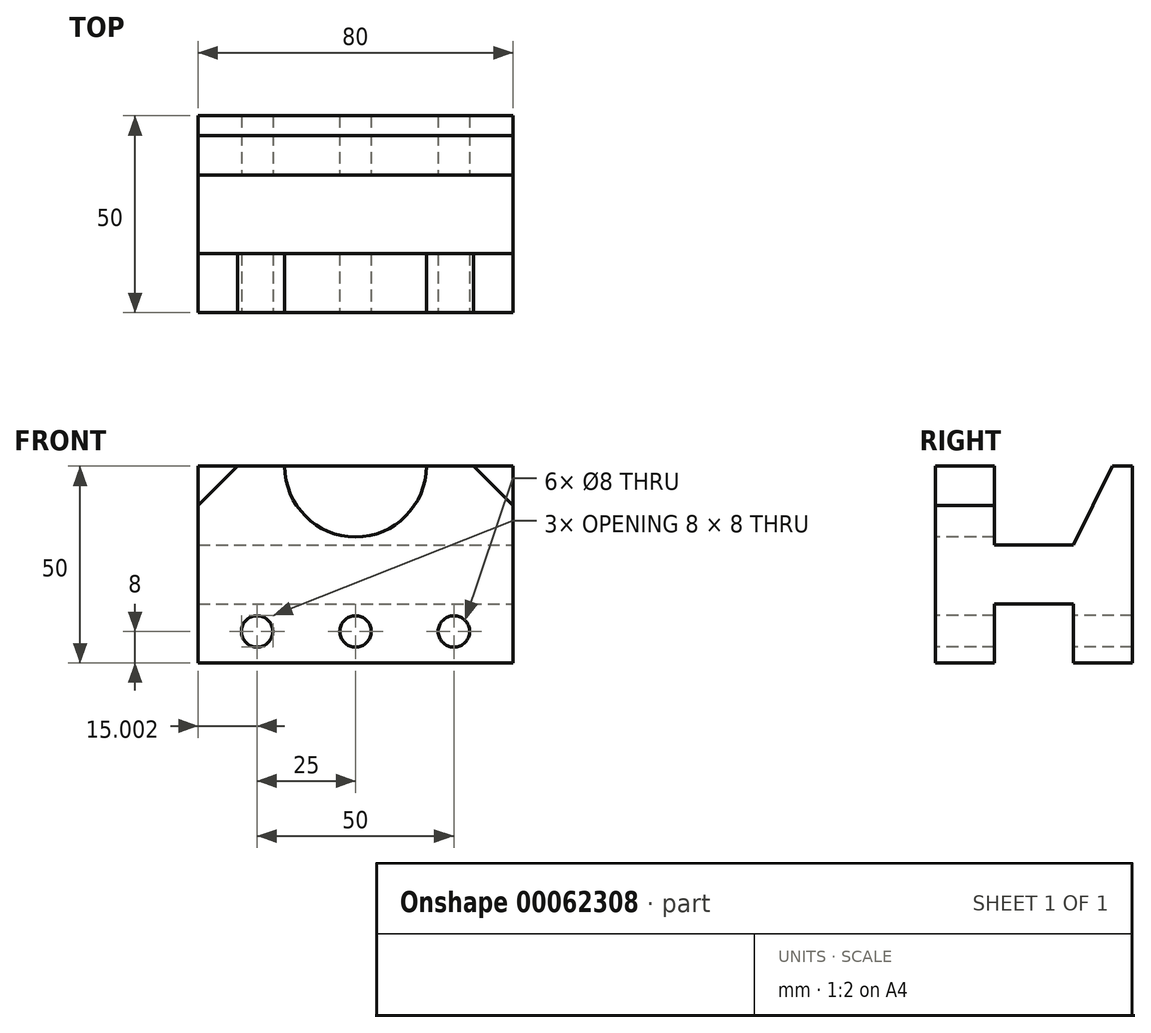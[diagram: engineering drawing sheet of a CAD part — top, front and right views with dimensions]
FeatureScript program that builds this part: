
annotation { "Feature Type Name" : "Feature", "Feature Type Description" : "" }
export const myFeature = defineFeature(function(context is Context, id is Id, definition is map)
    precondition{}
    {
        {
            var Q0;
            Q0=qCreatedBy(makeId("Top.planeOp"),FACE);
            var sketch = newSketch(context, id + "F0", { "sketchPlane" : qUnion([Q0])});
            skLineSegment(sketch, "E0.bottom", {"start": v(3.03, 0) * mm, "end": v(83.03, 0) * mm});
            skLineSegment(sketch, "E0.top", {"start": v(3.03, 50) * mm, "end": v(83.03, 50) * mm});
            skLineSegment(sketch, "E0.left", {"start": v(3.03, 0) * mm, "end": v(3.03, 50) * mm});
            skLineSegment(sketch, "E0.right", {"start": v(83.03, 0) * mm, "end": v(83.03, 50) * mm});
            skSolve(sketch);
        }
        {
            var Q0;
            Q0=makeQuery(id+"F0.imprint","IMPRINT",FACE,{"disambiguationData":[TD([[makeQuery(id+"F0.imprint","IMPRINT",EDGE,{"derivedFrom":sQuery(id+"F0.wireOp",EDGE,"E0.bottom")}),1.0]])]});
            extrude(context, id + "F1", {"entities" : qUnion([Q0]), "depth" : 50 * mm});
        }
        {
            var Q0;
            Q0=makeQuery(id+"F1.opExtrude","SWEPT_FACE",FACE,{"disambiguationData":[OSD([sQuery(id+"F0.wireOp",EDGE,"E0.right")])]});
            var sketch = newSketch(context, id + "F2", { "sketchPlane" : qUnion([Q0])});
            skLineSegment(sketch, "E1.bottom", {"start": v(15, 0) * mm, "end": v(35, 0) * mm});
            skLineSegment(sketch, "E1.top", {"start": v(15, 15) * mm, "end": v(35, 15) * mm});
            skLineSegment(sketch, "E1.left", {"start": v(15, 0) * mm, "end": v(15, 15) * mm});
            skLineSegment(sketch, "E1.right", {"start": v(35, 0) * mm, "end": v(35, 15) * mm});
            skSolve(sketch);
        }
        {
            var Q0;
            Q0=makeQuery(id+"F2.imprint","IMPRINT",FACE,{"disambiguationData":[TD([[makeQuery(id+"F2.imprint","IMPRINT",EDGE,{"derivedFrom":sQuery(id+"F2.wireOp",EDGE,"E1.bottom")}),1.0]])]});
            extrude(context, id + "F3", {"entities" : qUnion([Q0]), "operationType" : NewBodyOperationType.REMOVE, "oppositeDirection" : true, "depth" : 80 * mm});
        }
        {
            var Q0;
            Q0=makeQuery(id+"F1.opExtrude","SWEPT_FACE",FACE,{"disambiguationData":[OSD([sQuery(id+"F0.wireOp",EDGE,"E0.right")])]});
            var sketch = newSketch(context, id + "F4", { "sketchPlane" : qUnion([Q0])});
            skLineSegment(sketch, "E2.bottom", {"start": v(15, 50) * mm, "end": v(45, 50) * mm});
            skLineSegment(sketch, "E2.top", {"start": v(15, 30) * mm, "end": v(35, 30) * mm});
            skLineSegment(sketch, "E2.left", {"start": v(15, 50) * mm, "end": v(15, 30) * mm});
            skLineSegment(sketch, "E3", {"start": v(35, 30) * mm, "end": v(45, 50) * mm});
            skSolve(sketch);
        }
        {
            var Q0;
            Q0=makeQuery(id+"F4.imprint","IMPRINT",FACE,{"disambiguationData":[TD([[makeQuery(id+"F4.imprint","IMPRINT",EDGE,{"derivedFrom":sQuery(id+"F4.wireOp",EDGE,"E2.bottom")}),-1.0]])]});
            extrude(context, id + "F5", {"entities" : qUnion([Q0]), "operationType" : NewBodyOperationType.REMOVE, "oppositeDirection" : true, "depth" : 80 * mm});
        }
        {
            var Q0;
            Q0=makeQuery(id+"F1.opExtrude","SWEPT_FACE",FACE,{"disambiguationData":[OSD([sQuery(id+"F0.wireOp",EDGE,"E0.bottom")])]});
            var sketch = newSketch(context, id + "F6", { "sketchPlane" : qUnion([Q0])});
            skArc(sketch, "E4", {"start": v(25.03, 50) * mm, "mid": v(43.03, 32) * mm, "end": v(61.03, 50) * mm});
            skLineSegment(sketch, "E5", {"start": v(25.03, 50) * mm, "end": v(61.03, 50) * mm});
            skSolve(sketch);
        }
        {
            var Q0;
            Q0 = qSketchRegion(id + "F6", true);
            extrude(context, id + "F7", {"entities" : qUnion([Q0]), "operationType" : NewBodyOperationType.REMOVE, "oppositeDirection" : true, "depth" : 25 * mm});
        }
        {
            var Q0;
            {var subQ0=sQuery(id+"F0.wireOp",EDGE,"E0.bottom");var subQ1=sQuery(id+"F0.wireOp",EDGE,"E0.right");Q0=makeQuery(id+"F5.boolean.opBoolean","SPLIT",EDGE,{"disambiguationData":[TD([makeQuery(id+"F1.opExtrude","SWEPT_FACE",FACE,{"disambiguationData":[OSD([subQ0])]})])],"derivedFrom":makeQuery(id+"F1.opExtrude","CAP_EDGE",EDGE,{"disambiguationData":[OSD([subQ1])],"isStart":false})});}
            chamfer(context, id + "F8", {"entities" : qUnion([Q0]), "width" : 10 * mm, "tangentPropagation" : true});
        }
        {
            var Q0;
            {var subQ0=sQuery(id+"F0.wireOp",EDGE,"E0.bottom");var subQ1=sQuery(id+"F0.wireOp",EDGE,"E0.left");Q0=makeQuery(id+"F5.boolean.opBoolean","SPLIT",EDGE,{"disambiguationData":[TD([makeQuery(id+"F1.opExtrude","SWEPT_FACE",FACE,{"disambiguationData":[OSD([subQ0])]})])],"derivedFrom":makeQuery(id+"F1.opExtrude","CAP_EDGE",EDGE,{"disambiguationData":[OSD([subQ1])],"isStart":false})});}
            chamfer(context, id + "F9", {"entities" : qUnion([Q0]), "width" : 10 * mm, "tangentPropagation" : true});
        }
        {
            var Q0;
            Q0=makeQuery(id+"F1.opExtrude","SWEPT_FACE",FACE,{"disambiguationData":[OSD([sQuery(id+"F0.wireOp",EDGE,"E0.bottom")])]});
            var sketch = newSketch(context, id + "F10", { "sketchPlane" : qUnion([Q0])});
            skCircle(sketch, "E6", {"center": v(18.03, 8) * mm, "radius": 4 * mm});
            skCircle(sketch, "E7", {"center": v(43.03, 8) * mm, "radius": 4 * mm});
            skCircle(sketch, "E8", {"center": v(68.03, 8) * mm, "radius": 4 * mm});
            skSolve(sketch);
        }
        {
            var Q0;
            Q0=makeQuery(id+"F10.imprint","IMPRINT",FACE,{"disambiguationData":[TD([[makeQuery(id+"F10.imprint","IMPRINT",EDGE,{"derivedFrom":sQuery(id+"F10.wireOp",EDGE,"E6")}),1.0]])]});
            var Q1;
            Q1=makeQuery(id+"F10.imprint","IMPRINT",FACE,{"disambiguationData":[TD([[makeQuery(id+"F10.imprint","IMPRINT",EDGE,{"derivedFrom":sQuery(id+"F10.wireOp",EDGE,"E7")}),1.0]])]});
            var Q2;
            Q2=makeQuery(id+"F10.imprint","IMPRINT",FACE,{"disambiguationData":[TD([[makeQuery(id+"F10.imprint","IMPRINT",EDGE,{"derivedFrom":sQuery(id+"F10.wireOp",EDGE,"E8")}),1.0]])]});
            extrude(context, id + "F11", {"entities" : qUnion([Q0, Q1, Q2]), "operationType" : NewBodyOperationType.REMOVE, "oppositeDirection" : true, "depth" : 50 * mm});
        }
    });
